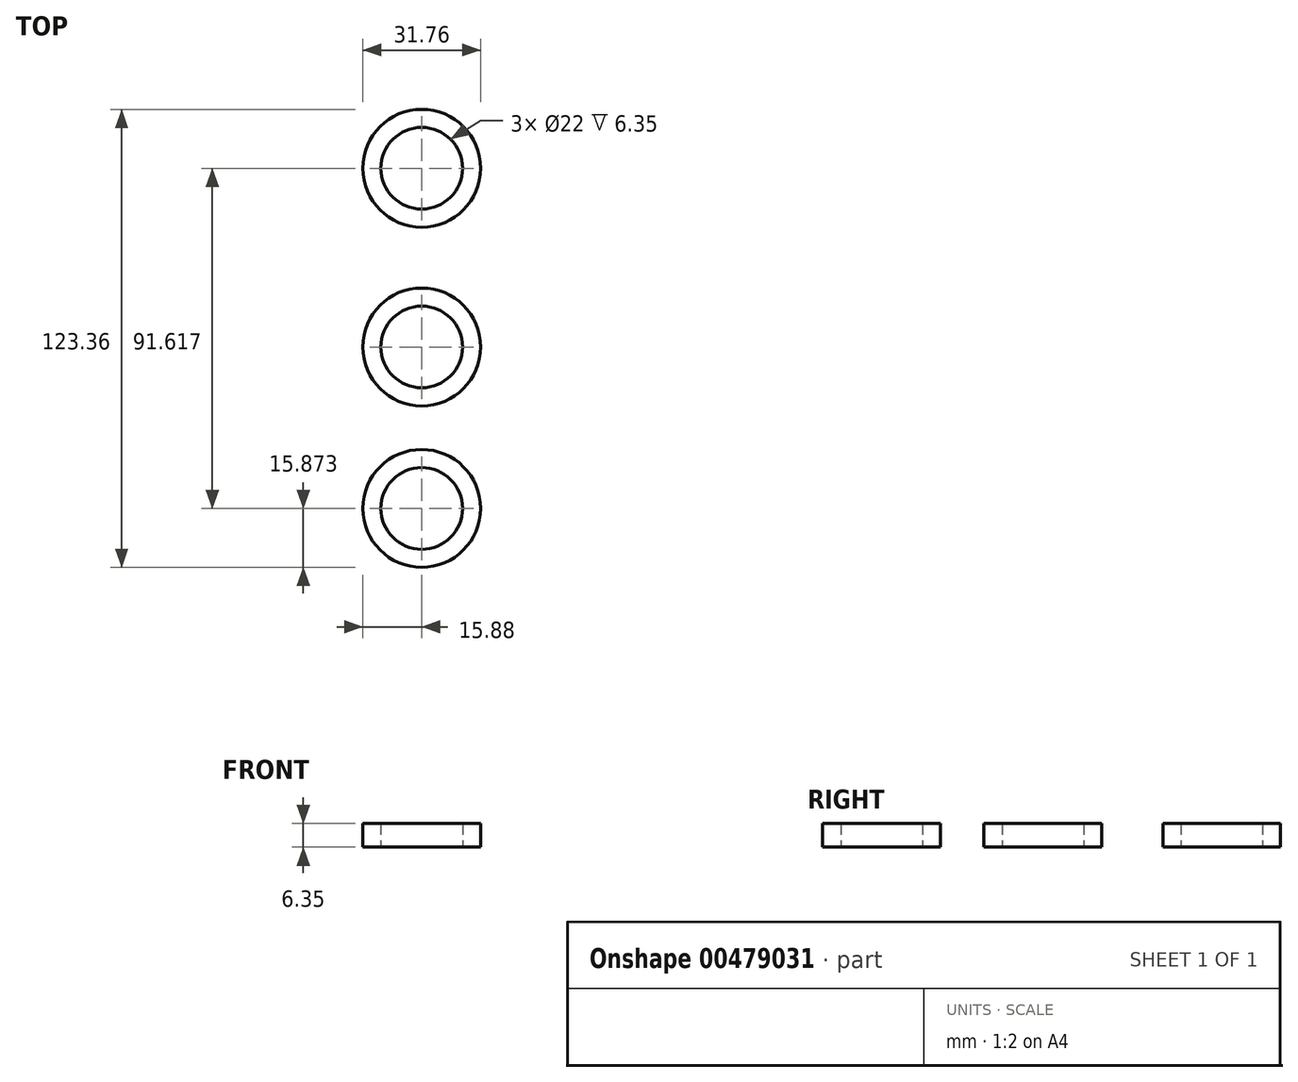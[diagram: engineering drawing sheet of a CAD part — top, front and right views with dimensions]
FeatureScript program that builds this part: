
annotation { "Feature Type Name" : "Feature", "Feature Type Description" : "" }
export const myFeature = defineFeature(function(context is Context, id is Id, definition is map)
    precondition{}
    {
        {
            var Q0;
            Q0=qCreatedBy(makeId("Top.planeOp"),FACE);
            var sketch = newSketch(context, id + "F0", { "sketchPlane" : qUnion([Q0])});
            skCircle(sketch, "E0", {"center": v(0, 0) * mm, "radius": 15.88 * mm});
            skCircle(sketch, "E1", {"center": v(0, 0) * mm, "radius": 11 * mm});
            skSolve(sketch);
        }
        {
            var Q0;
            Q0=qCreatedBy(makeId("Top.planeOp"),FACE);
            var sketch = newSketch(context, id + "F1", { "sketchPlane" : qUnion([Q0])});
            skCircle(sketch, "E2", {"center": v(0, 48.13) * mm, "radius": 15.88 * mm});
            skCircle(sketch, "E3", {"center": v(0, -43.49) * mm, "radius": 15.88 * mm});
            skCircle(sketch, "E4", {"center": v(0, -43.49) * mm, "radius": 11 * mm});
            skCircle(sketch, "E5", {"center": v(0, 48.13) * mm, "radius": 11 * mm});
            skSolve(sketch);
        }
        {
            var Q0;
            Q0=makeQuery(id+"F1.imprint","IMPRINT",FACE,{"disambiguationData":[TD([[makeQuery(id+"F1.imprint","IMPRINT",EDGE,{"derivedFrom":sQuery(id+"F1.wireOp",EDGE,"E2")}),1.0]])]});
            var Q1;
            Q1=makeQuery(id+"F0.imprint","IMPRINT",FACE,{"disambiguationData":[TD([[makeQuery(id+"F0.imprint","IMPRINT",EDGE,{"derivedFrom":sQuery(id+"F0.wireOp",EDGE,"E0")}),1.0]])]});
            var Q2;
            Q2=makeQuery(id+"F1.imprint","IMPRINT",FACE,{"disambiguationData":[TD([[makeQuery(id+"F1.imprint","IMPRINT",EDGE,{"derivedFrom":sQuery(id+"F1.wireOp",EDGE,"E3")}),1.0]])]});
            extrude(context, id + "F2", {"entities" : qUnion([Q0, Q1, Q2]), "depth" : 6.35 * mm});
        }
    });
